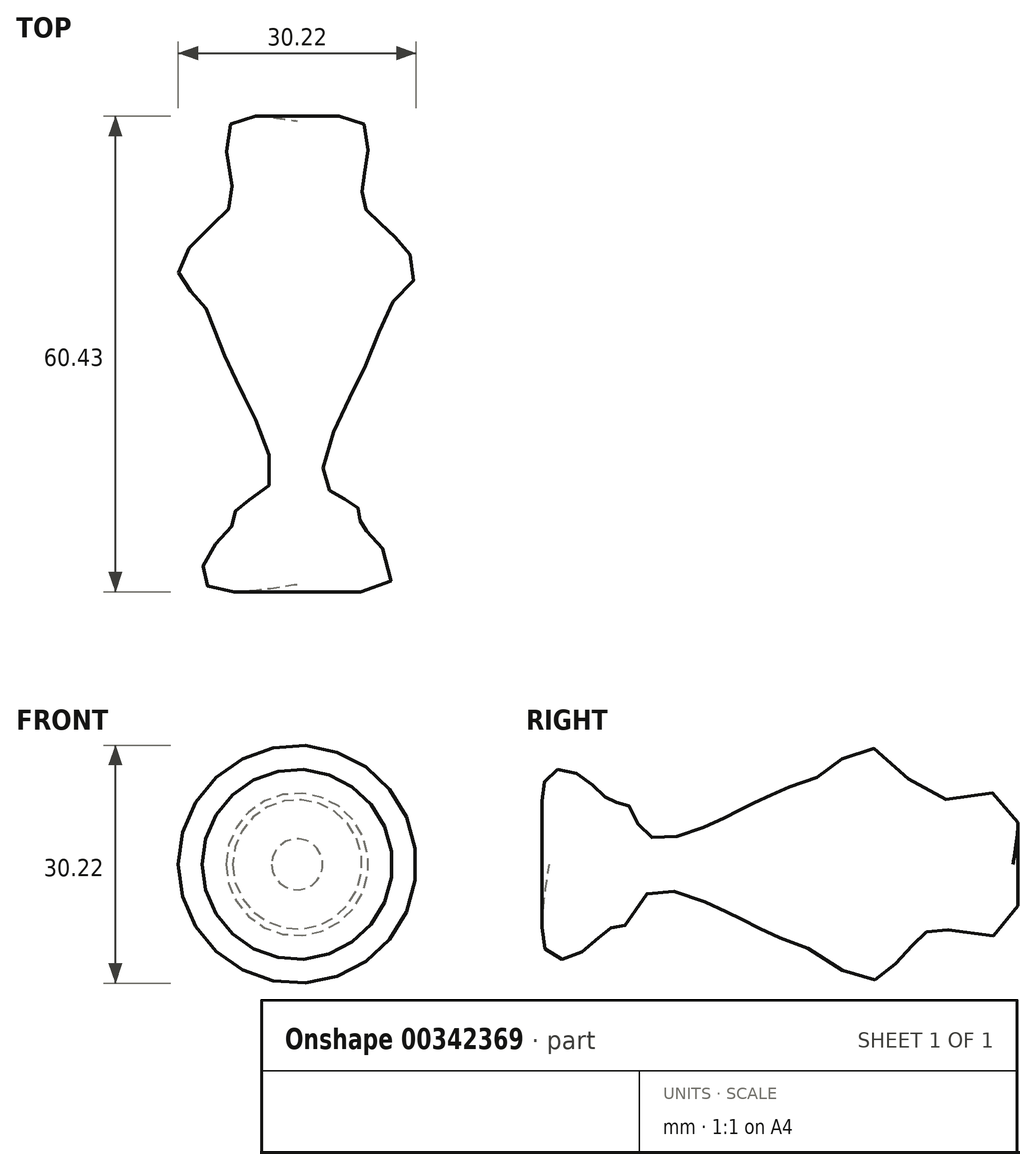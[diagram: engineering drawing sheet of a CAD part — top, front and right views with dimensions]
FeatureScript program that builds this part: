
annotation { "Feature Type Name" : "Feature", "Feature Type Description" : "" }
export const myFeature = defineFeature(function(context is Context, id is Id, definition is map)
    precondition{}
    {
        {
            var Q0;
            Q0=qCreatedBy(makeId("Top.planeOp"),FACE);
            var sketch = newSketch(context, id + "F0", { "sketchPlane" : qUnion([Q0])});
            skFitSpline(sketch, "E0", {"points": [v(0, 0) * mm, v(-11.56, 0) * mm, v(-11.11, 4.22) * mm, v(-8, 8) * mm, v(-7.56, 10) * mm, v(-3.56, 12.67) * mm, v(-6, 22.45) * mm, v(-7.56, 25.56) * mm, v(-10.22, 31.56) * mm, v(-12.22, 36) * mm, v(-15.11, 39.78) * mm, v(-10.45, 46) * mm, v(-8.22, 49.34) * mm, v(-8.67, 58.23) * mm, v(0, 58.9) * mm], "startDerivative": vector(-150.98, -23.68) * mm, "endDerivative": vector(130.97, -21.84) * mm});
            skLineSegment(sketch, "E1", {"start": v(0, 58.9) * mm, "end": v(0, 0) * mm});
            skSolve(sketch);
        }
        {
            var Q0;
            Q0=makeQuery(id+"F0.imprint","IMPRINT",FACE,{"disambiguationData":[TD([[makeQuery(id+"F0.imprint","IMPRINT",EDGE,{"derivedFrom":sQuery(id+"F0.wireOp",EDGE,"E0")}),-1.0]])]});
            var Q1;
            Q1=sQuery(id+"F0.wireOp",EDGE,"E1");
            revolve(context, id + "F1", {"entities" : qUnion([Q0]), "axis" : qUnion([Q1]), "revolveType" : RevolveType.FULL});
        }
    });
